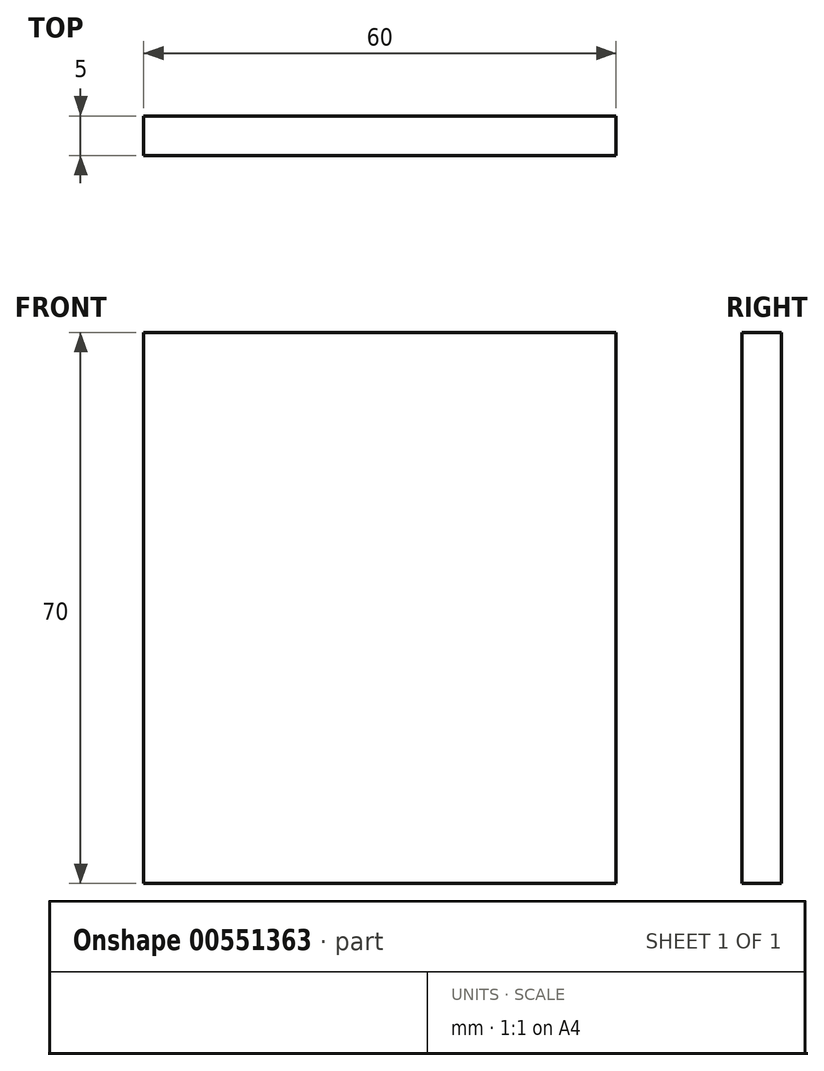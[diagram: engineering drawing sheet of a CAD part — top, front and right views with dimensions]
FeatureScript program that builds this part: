
annotation { "Feature Type Name" : "Feature", "Feature Type Description" : "" }
export const myFeature = defineFeature(function(context is Context, id is Id, definition is map)
    precondition{}
    {
        {
            var Q0;
            Q0=qCreatedBy(makeId("Front.planeOp"),FACE);
            var sketch = newSketch(context, id + "F0", { "sketchPlane" : qUnion([Q0])});
            skLineSegment(sketch, "E0.bottom", {"start": v(-114.03, 79.89) * mm, "end": v(-54.03, 79.89) * mm});
            skLineSegment(sketch, "E0.top", {"start": v(-114.03, 9.89) * mm, "end": v(-54.03, 9.89) * mm});
            skLineSegment(sketch, "E0.left", {"start": v(-114.03, 79.89) * mm, "end": v(-114.03, 9.89) * mm});
            skLineSegment(sketch, "E0.right", {"start": v(-54.03, 79.89) * mm, "end": v(-54.03, 9.89) * mm});
            skSolve(sketch);
        }
        {
            var Q0;
            Q0 = qSketchRegion(id + "F0", true);
            extrude(context, id + "F1", {"entities" : qUnion([Q0]), "depth" : 5 * mm, "offsetDistance" : 25 * mm});
        }
    });
